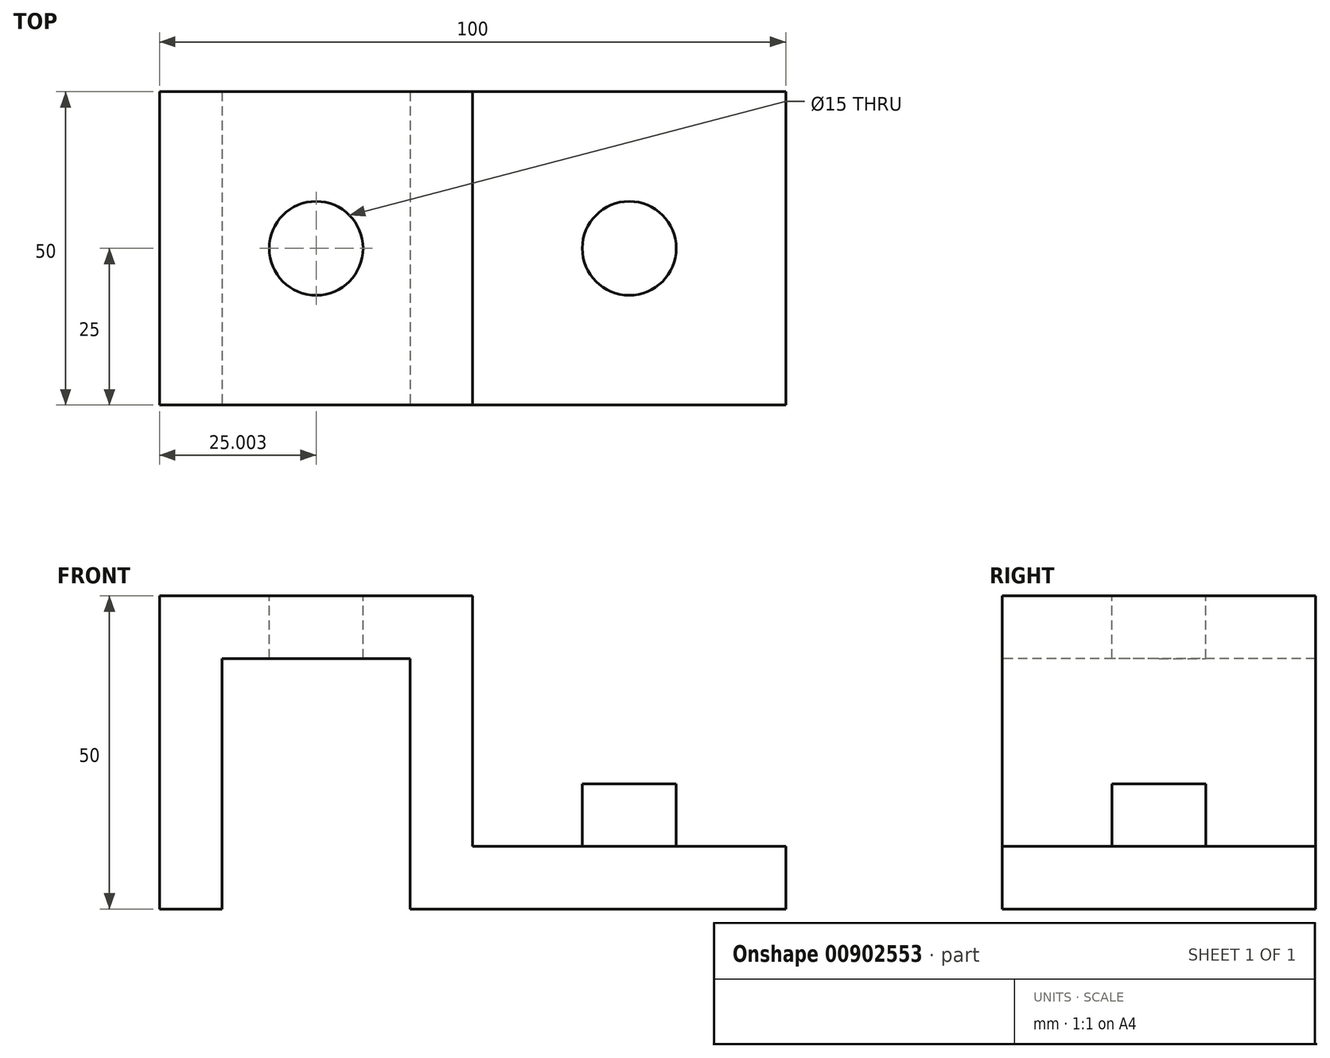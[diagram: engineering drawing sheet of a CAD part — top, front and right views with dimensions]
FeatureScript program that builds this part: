
annotation { "Feature Type Name" : "Feature", "Feature Type Description" : "" }
export const myFeature = defineFeature(function(context is Context, id is Id, definition is map)
    precondition{}
    {
        {
            var Q0;
            Q0=qCreatedBy(makeId("Top.planeOp"),FACE);
            var sketch = newSketch(context, id + "F0", { "sketchPlane" : qUnion([Q0])});
            skLineSegment(sketch, "E0", {"start": v(-75.85, 0) * mm, "end": v(73.6, 0) * mm, "construction": true});
            skLineSegment(sketch, "E1", {"start": v(10.61, 27.28) * mm, "end": v(10.61, -19.98) * mm, "construction": true});
            skLineSegment(sketch, "E2.0", {"start": v(-39.39, 27.28) * mm, "end": v(-39.39, -19.98) * mm, "construction": true});
            skLineSegment(sketch, "E3.0", {"start": v(-64.39, 25) * mm, "end": v(35.61, 25) * mm});
            skLineSegment(sketch, "E4.0", {"start": v(-64.39, 25) * mm, "end": v(-64.39, -25) * mm});
            skLineSegment(sketch, "E5.0", {"start": v(35.61, 25) * mm, "end": v(35.61, -25) * mm});
            skLineSegment(sketch, "E6.MirrorCS", {"start": v(-64.39, -25) * mm, "end": v(35.61, -25) * mm});
            skPoint(sketch, "E7.newPointA", {"position": v(-75.85, 25) * mm});
            skLineSegment(sketch, "E7.filletArc", {"start": v(-64.39, 25) * mm, "end": v(-64.39, 25) * mm});
            skPoint(sketch, "E8.newPointB", {"position": v(-75.85, -25) * mm});
            skLineSegment(sketch, "E8.filletArc", {"start": v(-64.39, -25) * mm, "end": v(-64.39, -25) * mm});
            skPoint(sketch, "E9.newPointA", {"position": v(73.6, 25) * mm});
            skLineSegment(sketch, "E9.filletArc", {"start": v(35.61, 25) * mm, "end": v(35.61, 25) * mm});
            skPoint(sketch, "E10.newPointB", {"position": v(73.6, -25) * mm});
            skLineSegment(sketch, "E10.filletArc", {"start": v(35.61, -25) * mm, "end": v(35.61, -25) * mm});
            skCircle(sketch, "E11", {"center": v(-39.39, 0) * mm, "radius": 7.5 * mm, "construction": true});
            skCircle(sketch, "E12", {"center": v(10.61, 0) * mm, "radius": 7.5 * mm, "construction": true});
            skSolve(sketch);
        }
        {
            var Q0;
            Q0=makeQuery(id+"F0.imprint","IMPRINT",FACE,{"disambiguationData":[TD([[makeQuery(id+"F0.imprint","IMPRINT",EDGE,{"derivedFrom":sQuery(id+"F0.wireOp",EDGE,"E3.0")}),-1.0]])]});
            extrude(context, id + "F1", {"entities" : qUnion([Q0]), "depth" : 50 * mm, "offsetDistance" : 25 * mm});
        }
        {
            var Q0;
            Q0=makeQuery(id+"F1.opExtrude","SWEPT_FACE",FACE,{"disambiguationData":[OSD([sQuery(id+"F0.wireOp",EDGE,"E6.MirrorCS")])]});
            var sketch = newSketch(context, id + "F2", { "sketchPlane" : qUnion([Q0])});
            skLineSegment(sketch, "E13.bottom", {"start": v(-14.39, 50) * mm, "end": v(35.61, 50) * mm});
            skLineSegment(sketch, "E13.top", {"start": v(-14.39, 10) * mm, "end": v(35.61, 10) * mm});
            skLineSegment(sketch, "E13.left", {"start": v(-14.39, 50) * mm, "end": v(-14.39, 10) * mm});
            skLineSegment(sketch, "E13.right", {"start": v(35.61, 50) * mm, "end": v(35.61, 10) * mm});
            skSolve(sketch);
        }
        {
            var Q0;
            Q0=makeQuery(id+"F2.imprint","IMPRINT",FACE,{"disambiguationData":[TD([[makeQuery(id+"F2.imprint","IMPRINT",EDGE,{"derivedFrom":sQuery(id+"F2.wireOp",EDGE,"E13.bottom")}),-1.0]])]});
            extrude(context, id + "F3", {"entities" : qUnion([Q0]), "operationType" : NewBodyOperationType.REMOVE, "endBound" : BoundingType.THROUGH_ALL, "oppositeDirection" : true, "depth" : 25 * mm, "offsetDistance" : 25 * mm});
        }
        {
            var Q0;
            Q0=makeQuery(id+"F1.opExtrude","SWEPT_FACE",FACE,{"disambiguationData":[OSD([sQuery(id+"F0.wireOp",EDGE,"E6.MirrorCS")])]});
            var sketch = newSketch(context, id + "F4", { "sketchPlane" : qUnion([Q0])});
            skLineSegment(sketch, "E14.bottom", {"start": v(-54.39, 0) * mm, "end": v(-24.39, 0) * mm});
            skLineSegment(sketch, "E14.top", {"start": v(-54.39, 40) * mm, "end": v(-24.39, 40) * mm});
            skLineSegment(sketch, "E14.left", {"start": v(-54.39, 0) * mm, "end": v(-54.39, 40) * mm});
            skLineSegment(sketch, "E14.right", {"start": v(-24.39, 0) * mm, "end": v(-24.39, 40) * mm});
            skSolve(sketch);
        }
        {
            var Q0;
            Q0=makeQuery(id+"F4.imprint","IMPRINT",FACE,{"disambiguationData":[TD([[makeQuery(id+"F4.imprint","IMPRINT",EDGE,{"derivedFrom":sQuery(id+"F4.wireOp",EDGE,"E14.bottom")}),1.0]])]});
            extrude(context, id + "F5", {"entities" : qUnion([Q0]), "operationType" : NewBodyOperationType.REMOVE, "endBound" : BoundingType.THROUGH_ALL, "oppositeDirection" : true, "depth" : 25 * mm, "offsetDistance" : 25 * mm});
        }
        {
            var Q0;
            Q0=makeQuery(id+"F1.opExtrude","CAP_FACE",FACE,{"disambiguationData":[OSD([sQuery(id+"F0.wireOp",EDGE,"E3.0"),sQuery(id+"F0.wireOp",EDGE,"E4.0"),sQuery(id+"F0.wireOp",EDGE,"E5.0"),sQuery(id+"F0.wireOp",EDGE,"E6.MirrorCS")])],"isStart":false});
            var sketch = newSketch(context, id + "F6", { "sketchPlane" : qUnion([Q0])});
            skCircle(sketch, "E15", {"center": v(-39.39, 0) * mm, "radius": 7.5 * mm});
            skSolve(sketch);
        }
        {
            var Q0;
            Q0=makeQuery(id+"F6.imprint","IMPRINT",FACE,{"disambiguationData":[TD([[makeQuery(id+"F6.imprint","IMPRINT",EDGE,{"derivedFrom":sQuery(id+"F6.wireOp",EDGE,"E15")}),1.0]])]});
            extrude(context, id + "F7", {"entities" : qUnion([Q0]), "operationType" : NewBodyOperationType.REMOVE, "endBound" : BoundingType.THROUGH_ALL, "oppositeDirection" : true, "depth" : 25 * mm, "offsetDistance" : 25 * mm});
        }
        {
            var Q0;
            Q0=makeQuery(id+"F0.imprint","IMPRINT",FACE,{"disambiguationData":[TD([[makeQuery(id+"F0.imprint","IMPRINT",EDGE,{"derivedFrom":sQuery(id+"F0.wireOp",EDGE,"E3.0")}),-1.0]])]});
            var sketch = newSketch(context, id + "F8", { "sketchPlane" : qUnion([Q0])});
            skCircle(sketch, "E16", {"center": v(10.61, 0) * mm, "radius": 7.5 * mm});
            skSolve(sketch);
        }
        {
            var Q0;
            Q0 = qSketchRegion(id + "F8", true);
            extrude(context, id + "F9", {"entities" : qUnion([Q0]), "operationType" : NewBodyOperationType.ADD, "depth" : 20 * mm, "offsetDistance" : 25 * mm});
        }
    });
